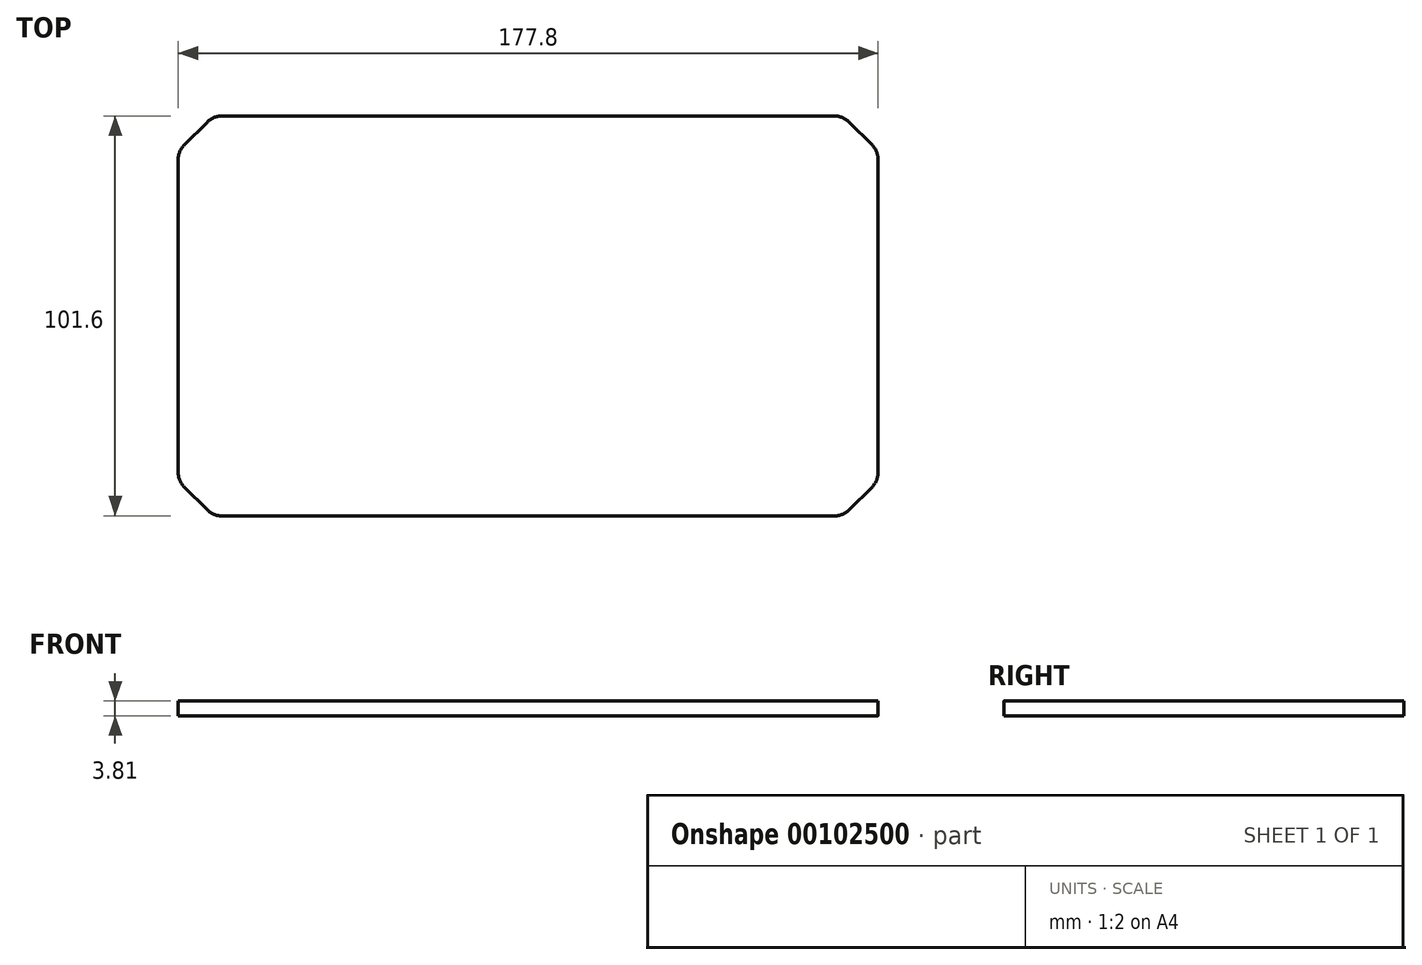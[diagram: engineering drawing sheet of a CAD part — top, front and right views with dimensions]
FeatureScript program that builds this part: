
annotation { "Feature Type Name" : "Feature", "Feature Type Description" : "" }
export const myFeature = defineFeature(function(context is Context, id is Id, definition is map)
    precondition{}
    {
        {
            var Q0;
            Q0=qCreatedBy(makeId("Top.planeOp"),FACE);
            var sketch = newSketch(context, id + "F0", { "sketchPlane" : qUnion([Q0])});
            skLineSegment(sketch, "E0.bottom", {"start": v(-80, 50.8) * mm, "end": v(80, 50.8) * mm});
            skLineSegment(sketch, "E0.top", {"start": v(-80.01, -50.8) * mm, "end": v(80, -50.8) * mm});
            skLineSegment(sketch, "E0.left", {"start": v(-88.9, 41.9) * mm, "end": v(-88.9, -41.9) * mm});
            skLineSegment(sketch, "E0.right", {"start": v(88.9, 41.9) * mm, "end": v(88.9, -41.9) * mm});
            skLineSegment(sketch, "E1", {"start": v(80, 50.8) * mm, "end": v(88.9, 41.9) * mm});
            skLineSegment(sketch, "E2", {"start": v(-80, 50.8) * mm, "end": v(-88.9, 41.9) * mm});
            skLineSegment(sketch, "E3", {"start": v(-88.9, -41.9) * mm, "end": v(-80.01, -50.8) * mm});
            skLineSegment(sketch, "E4", {"start": v(80.01, -50.8) * mm, "end": v(88.9, -41.9) * mm});
            skSolve(sketch);
        }
        {
            var Q0;
            Q0=makeQuery(id+"F0.imprint","IMPRINT",FACE,{"disambiguationData":[TD([[makeQuery(id+"F0.imprint","IMPRINT",EDGE,{"derivedFrom":sQuery(id+"F0.wireOp",EDGE,"E0.bottom")}),-1.0]])]});
            extrude(context, id + "F1", {"entities" : qUnion([Q0]), "depth" : 3.8 * mm});
        }
        {
            var Q0;
            Q0=makeQuery(id+"F1.opExtrude","SWEPT_EDGE",EDGE,{"disambiguationData":[OSD([sQuery(id+"F0.wireOp",EDGE,"E0.top"),sQuery(id+"F0.wireOp",EDGE,"E3")])]});
            var Q1;
            Q1=makeQuery(id+"F1.opExtrude","SWEPT_EDGE",EDGE,{"disambiguationData":[OSD([sQuery(id+"F0.wireOp",EDGE,"E0.left"),sQuery(id+"F0.wireOp",EDGE,"E3")])]});
            var Q2;
            Q2=makeQuery(id+"F1.opExtrude","SWEPT_EDGE",EDGE,{"disambiguationData":[OSD([sQuery(id+"F0.wireOp",EDGE,"E0.bottom"),sQuery(id+"F0.wireOp",EDGE,"E2")])]});
            var Q3;
            Q3=makeQuery(id+"F1.opExtrude","SWEPT_EDGE",EDGE,{"disambiguationData":[OSD([sQuery(id+"F0.wireOp",EDGE,"E0.left"),sQuery(id+"F0.wireOp",EDGE,"E2")])]});
            var Q4;
            Q4=makeQuery(id+"F1.opExtrude","SWEPT_EDGE",EDGE,{"disambiguationData":[OSD([sQuery(id+"F0.wireOp",EDGE,"E0.bottom"),sQuery(id+"F0.wireOp",EDGE,"E1")])]});
            var Q5;
            Q5=makeQuery(id+"F1.opExtrude","SWEPT_EDGE",EDGE,{"disambiguationData":[OSD([sQuery(id+"F0.wireOp",EDGE,"E0.right"),sQuery(id+"F0.wireOp",EDGE,"E1")])]});
            var Q6;
            Q6=makeQuery(id+"F1.opExtrude","SWEPT_EDGE",EDGE,{"disambiguationData":[OSD([sQuery(id+"F0.wireOp",EDGE,"E0.right"),sQuery(id+"F0.wireOp",EDGE,"E4")])]});
            var Q7;
            Q7=makeQuery(id+"F1.opExtrude","SWEPT_EDGE",EDGE,{"disambiguationData":[OSD([sQuery(id+"F0.wireOp",EDGE,"E0.top"),sQuery(id+"F0.wireOp",EDGE,"E4")])]});
            fillet(context, id + "F2", {"entities" : qUnion([Q0, Q1, Q2, Q3, Q4, Q5, Q6, Q7]), "radius" : 5.08 * mm, "tangentPropagation" : true, "allowEdgeOverflow" : false});
        }
    });
